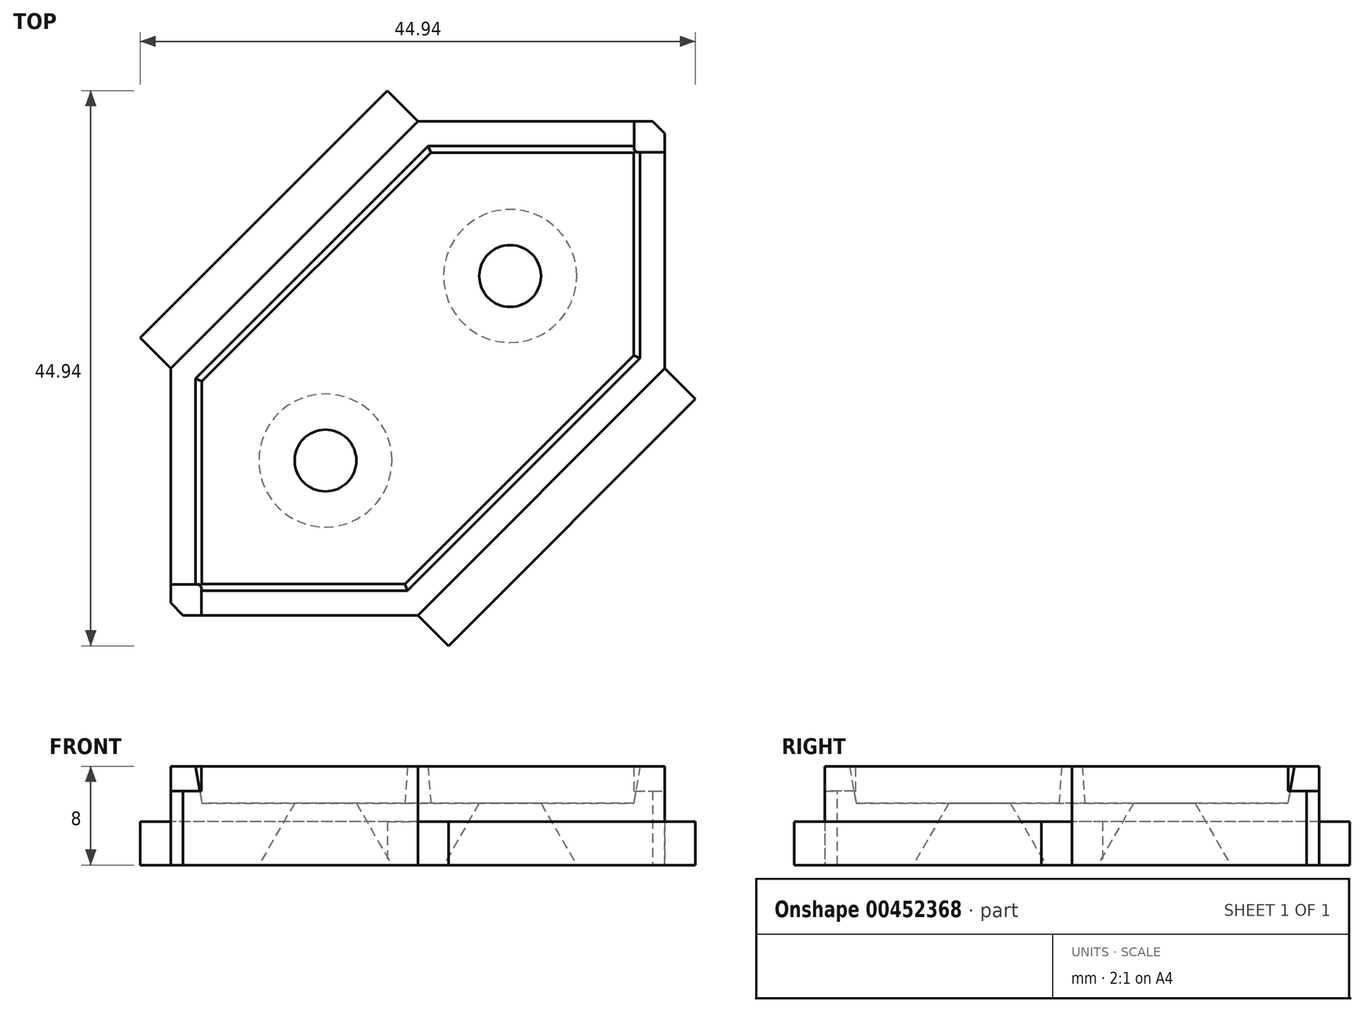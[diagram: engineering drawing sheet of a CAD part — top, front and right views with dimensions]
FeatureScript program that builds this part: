
annotation { "Feature Type Name" : "Feature", "Feature Type Description" : "" }
export const myFeature = defineFeature(function(context is Context, id is Id, definition is map)
    precondition{}
    {
        {
            var Q0;
            Q0=qCreatedBy(makeId("Top.planeOp"),FACE);
            var sketch = newSketch(context, id + "F0", { "sketchPlane" : qUnion([Q0])});
            skLineSegment(sketch, "E0.bottom", {"start": v(0, 0) * mm, "end": v(20, 0) * mm});
            skLineSegment(sketch, "E0.top", {"start": v(20, 40) * mm, "end": v(40, 40) * mm});
            skLineSegment(sketch, "E0.left", {"start": v(0, 0) * mm, "end": v(0, 20) * mm});
            skLineSegment(sketch, "E0.right", {"start": v(40, 20) * mm, "end": v(40, 40) * mm});
            skLineSegment(sketch, "E1", {"start": v(20, 40) * mm, "end": v(0, 20) * mm});
            skLineSegment(sketch, "E2", {"start": v(40, 20) * mm, "end": v(20, 0) * mm});
            skLineSegment(sketch, "E3", {"start": v(20, 40) * mm, "end": v(20, 0) * mm, "construction": true});
            skLineSegment(sketch, "E4", {"start": v(0, 0) * mm, "end": v(40, 40) * mm, "construction": true});
            skSolve(sketch);
        }
        {
            var Q0;
            Q0=qSketchRegion(id+"F0",true);
            extrude(context, id + "F1", {"entities" : qUnion([Q0]), "depth" : 8 * mm});
        }
        {
            var Q0;
            Q0=makeQuery(id+"F1.opExtrude","CAP_FACE",FACE,{"disambiguationData":[OSD([sQuery(id+"F0.wireOp",EDGE,"E0.bottom"),sQuery(id+"F0.wireOp",EDGE,"E0.top"),sQuery(id+"F0.wireOp",EDGE,"E0.left"),sQuery(id+"F0.wireOp",EDGE,"E0.right"),sQuery(id+"F0.wireOp",EDGE,"E1"),sQuery(id+"F0.wireOp",EDGE,"E2")])],"isStart":false});
            var sketch = newSketch(context, id + "F2", { "sketchPlane" : qUnion([Q0])});
            skLineSegment(sketch, "E5.bottom", {"start": v(2, 2) * mm, "end": v(19.17, 2) * mm});
            skLineSegment(sketch, "E5.top", {"start": v(20.83, 38) * mm, "end": v(38, 38) * mm});
            skLineSegment(sketch, "E5.left", {"start": v(2, 2) * mm, "end": v(2, 19.17) * mm});
            skLineSegment(sketch, "E5.right", {"start": v(38, 20.83) * mm, "end": v(38, 38) * mm});
            skLineSegment(sketch, "E6", {"start": v(20.83, 38) * mm, "end": v(2, 19.17) * mm});
            skLineSegment(sketch, "E7", {"start": v(38, 20.83) * mm, "end": v(19.17, 2) * mm});
            skSolve(sketch);
        }
        {
            var Q0;
            Q0=qSketchRegion(id+"F2",true);
            extrude(context, id + "F3", {"entities" : qUnion([Q0]), "operationType" : NewBodyOperationType.REMOVE, "oppositeDirection" : true, "depth" : 3 * mm, "hasDraft" : true, "draftAngle" : 10 * degree, "draftPullDirection" : true});
        }
        {
            var Q0;
            Q0=makeQuery(id+"F1.opExtrude","SWEPT_EDGE",EDGE,{"disambiguationData":[OSD([sQuery(id+"F0.wireOp",EDGE,"E0.bottom"),sQuery(id+"F0.wireOp",EDGE,"E0.left")])]});
            var Q1;
            Q1=makeQuery(id+"F1.opExtrude","SWEPT_EDGE",EDGE,{"disambiguationData":[OSD([sQuery(id+"F0.wireOp",EDGE,"E0.top"),sQuery(id+"F0.wireOp",EDGE,"E0.right")])]});
            chamfer(context, id + "F4", {"entities" : qUnion([Q0, Q1]), "width" : 1 * mm});
        }
        {
            var Q0;
            Q0=makeQuery(id+"F1.opExtrude","CAP_FACE",FACE,{"disambiguationData":[OSD([sQuery(id+"F0.wireOp",EDGE,"E0.bottom"),sQuery(id+"F0.wireOp",EDGE,"E0.top"),sQuery(id+"F0.wireOp",EDGE,"E0.left"),sQuery(id+"F0.wireOp",EDGE,"E0.right")])],"isStart":false});
            var sketch = newSketch(context, id + "F5", { "sketchPlane" : qUnion([Q0])});
            skLineSegment(sketch, "E8.bottom", {"start": v(0, 2.5) * mm, "end": v(2.5, 2.5) * mm});
            skLineSegment(sketch, "E8.top", {"start": v(0, 0) * mm, "end": v(2.5, 0) * mm});
            skLineSegment(sketch, "E8.left", {"start": v(0, 2.5) * mm, "end": v(0, 0) * mm});
            skLineSegment(sketch, "E8.right", {"start": v(2.5, 2.5) * mm, "end": v(2.5, 0) * mm});
            skLineSegment(sketch, "E9.bottom", {"start": v(37.5, 40) * mm, "end": v(40, 40) * mm});
            skLineSegment(sketch, "E9.top", {"start": v(37.5, 37.5) * mm, "end": v(40, 37.5) * mm});
            skLineSegment(sketch, "E9.left", {"start": v(40, 40) * mm, "end": v(40, 37.5) * mm});
            skLineSegment(sketch, "E9.right", {"start": v(37.5, 40) * mm, "end": v(37.5, 37.5) * mm});
            skSolve(sketch);
        }
        {
            var Q0;
            Q0=qSketchRegion(id+"F5",true);
            extrude(context, id + "F6", {"entities" : qUnion([Q0]), "operationType" : NewBodyOperationType.REMOVE, "oppositeDirection" : true, "depth" : 2 * mm});
        }
        {
            var Q0;
            Q0=makeQuery(id+"F3.boolean.opBoolean","COPY",FACE,{"derivedFrom":makeQuery(id+"F3.opExtrude","CAP_FACE",FACE,{"disambiguationData":[OSD([sQuery(id+"F2.wireOp",EDGE,"E5.bottom"),sQuery(id+"F2.wireOp",EDGE,"E5.top"),sQuery(id+"F2.wireOp",EDGE,"E5.left"),sQuery(id+"F2.wireOp",EDGE,"E5.right"),sQuery(id+"F2.wireOp",EDGE,"E6"),sQuery(id+"F2.wireOp",EDGE,"E7")])],"isStart":false})});
            var sketch = newSketch(context, id + "F7", { "sketchPlane" : qUnion([Q0])});
            skCircle(sketch, "E10", {"center": v(12.53, 12.53) * mm, "radius": 2.5 * mm});
            skCircle(sketch, "E11", {"center": v(27.47, 27.47) * mm, "radius": 2.5 * mm});
            skSolve(sketch);
        }
        {
            var Q0;
            Q0=qSketchRegion(id+"F7",true);
            extrude(context, id + "F8", {"entities" : qUnion([Q0]), "operationType" : NewBodyOperationType.REMOVE, "endBound" : BoundingType.UP_TO_NEXT, "oppositeDirection" : true, "depth" : 25 * mm, "hasDraft" : true, "draftAngle" : 30 * degree});
        }
        {
            var Q0;
            Q0=makeQuery(id+"F1.opExtrude","SWEPT_FACE",FACE,{"disambiguationData":[OSD([sQuery(id+"F0.wireOp",EDGE,"E2")])]});
            var sketch = newSketch(context, id + "F9", { "sketchPlane" : qUnion([Q0])});
            skLineSegment(sketch, "E12.bottom", {"start": v(14.14, 0) * mm, "end": v(42.43, 0) * mm});
            skLineSegment(sketch, "E12.top", {"start": v(14.14, 3.5) * mm, "end": v(42.43, 3.5) * mm});
            skLineSegment(sketch, "E12.left", {"start": v(14.14, 0) * mm, "end": v(14.14, 3.5) * mm});
            skLineSegment(sketch, "E12.right", {"start": v(42.43, 0) * mm, "end": v(42.43, 3.5) * mm});
            skSolve(sketch);
        }
        {
            var Q0;
            Q0=makeQuery(id+"F9.imprint","IMPRINT",FACE,{"disambiguationData":[TD([[makeQuery(id+"F9.imprint","IMPRINT",EDGE,{"derivedFrom":sQuery(id+"F9.wireOp",EDGE,"E12.bottom")}),-1.0]])]});
            extrude(context, id + "F10", {"entities" : qUnion([Q0]), "operationType" : NewBodyOperationType.ADD, "depth" : 3.5 * mm});
        }
        {
            var Q0;
            Q0=makeQuery(id+"F1.opExtrude","SWEPT_FACE",FACE,{"disambiguationData":[OSD([sQuery(id+"F0.wireOp",EDGE,"E1")])]});
            var sketch = newSketch(context, id + "F11", { "sketchPlane" : qUnion([Q0])});
            skLineSegment(sketch, "E13.bottom", {"start": v(-42.43, 3.5) * mm, "end": v(-14.14, 3.5) * mm});
            skLineSegment(sketch, "E13.top", {"start": v(-42.43, 0) * mm, "end": v(-14.14, 0) * mm});
            skLineSegment(sketch, "E13.left", {"start": v(-42.43, 3.5) * mm, "end": v(-42.43, 0) * mm});
            skLineSegment(sketch, "E13.right", {"start": v(-14.14, 3.5) * mm, "end": v(-14.14, 0) * mm});
            skSolve(sketch);
        }
        {
            var Q0;
            Q0=makeQuery(id+"F11.imprint","IMPRINT",FACE,{"disambiguationData":[TD([[makeQuery(id+"F11.imprint","IMPRINT",EDGE,{"derivedFrom":sQuery(id+"F11.wireOp",EDGE,"E13.bottom")}),-1.0]])]});
            extrude(context, id + "F12", {"entities" : qUnion([Q0]), "operationType" : NewBodyOperationType.ADD, "depth" : 3.5 * mm, "offsetDistance" : 25 * mm});
        }
    });
